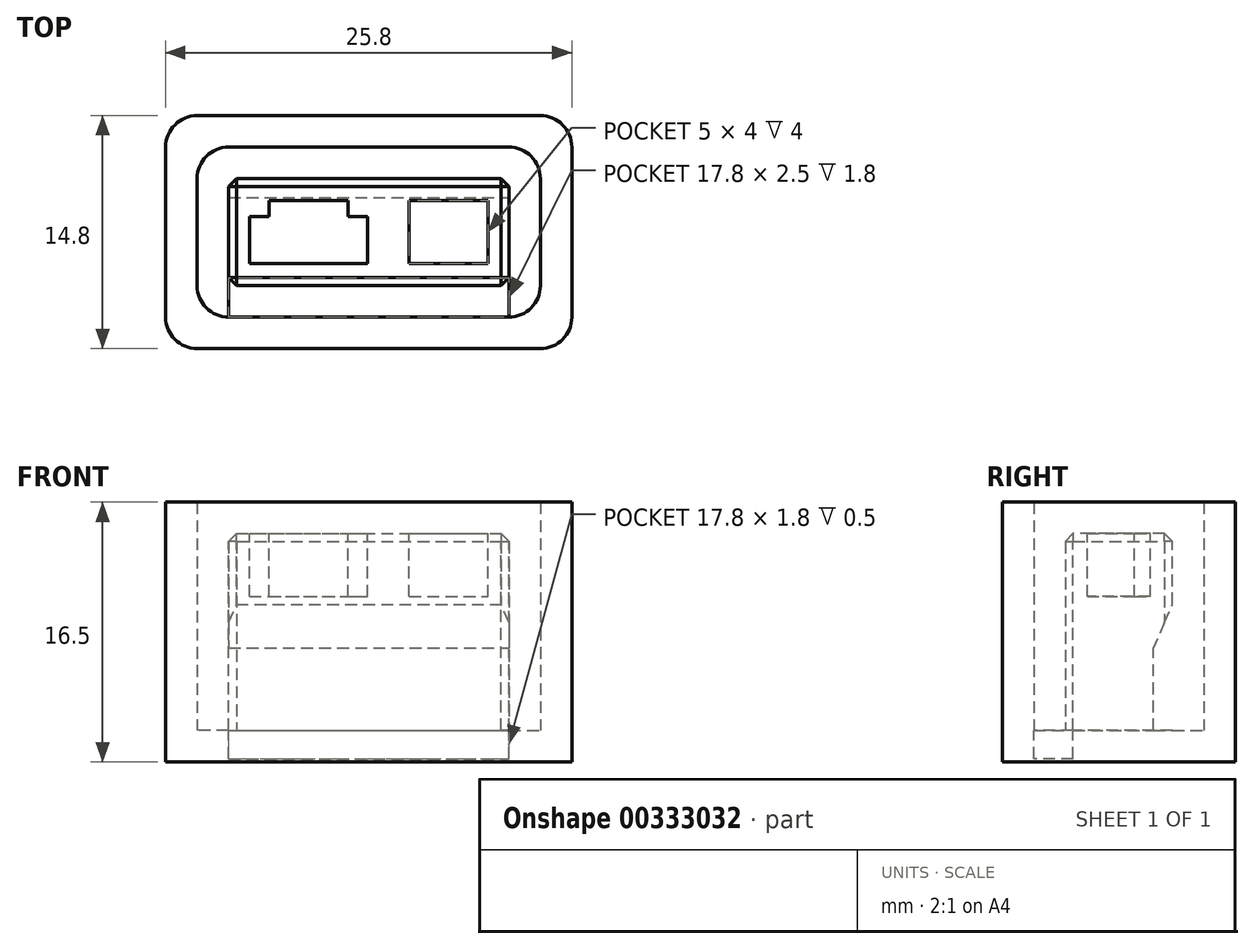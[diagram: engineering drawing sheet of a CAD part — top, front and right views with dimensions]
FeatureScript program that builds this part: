
annotation { "Feature Type Name" : "Feature", "Feature Type Description" : "" }
export const myFeature = defineFeature(function(context is Context, id is Id, definition is map)
    precondition{}
    {
        {
            var Q0;
            Q0=qCreatedBy(makeId("Top.planeOp"),FACE);
            var sketch = newSketch(context, id + "F0", { "sketchPlane" : qUnion([Q0])});
            skLineSegment(sketch, "E0.bottom", {"start": v(-12.9, 7.4) * mm, "end": v(12.9, 7.4) * mm});
            skLineSegment(sketch, "E0.top", {"start": v(-12.9, -7.4) * mm, "end": v(12.9, -7.4) * mm});
            skLineSegment(sketch, "E0.left", {"start": v(-12.9, 7.4) * mm, "end": v(-12.9, -7.4) * mm});
            skLineSegment(sketch, "E0.right", {"start": v(12.9, 7.4) * mm, "end": v(12.9, -7.4) * mm});
            skPoint(sketch, "E0.middle", {"position": v(0, 0) * mm});
            skSolve(sketch);
        }
        {
            var Q0;
            Q0 = qSketchRegion(id + "F0", true);
            extrude(context, id + "F1", {"entities" : qUnion([Q0]), "depth" : 2 * mm});
        }
        {
            var Q0;
            Q0=makeQuery(id+"F1.opExtrude","CAP_FACE",FACE,{"disambiguationData":[OSD([sQuery(id+"F0.wireOp",EDGE,"E0.bottom"),sQuery(id+"F0.wireOp",EDGE,"E0.top"),sQuery(id+"F0.wireOp",EDGE,"E0.left"),sQuery(id+"F0.wireOp",EDGE,"E0.right")])],"isStart":false});
            var sketch = newSketch(context, id + "F2", { "sketchPlane" : qUnion([Q0])});
            skLineSegment(sketch, "E1.bottom", {"start": v(-12.9, 7.4) * mm, "end": v(12.9, 7.4) * mm});
            skLineSegment(sketch, "E1.top", {"start": v(-12.9, -7.4) * mm, "end": v(12.9, -7.4) * mm});
            skLineSegment(sketch, "E1.left", {"start": v(-12.9, 7.4) * mm, "end": v(-12.9, -7.4) * mm});
            skLineSegment(sketch, "E1.right", {"start": v(12.9, 7.4) * mm, "end": v(12.9, -7.4) * mm});
            skPoint(sketch, "E1.middle", {"position": v(0, 0) * mm});
            skLineSegment(sketch, "E2.bottom", {"start": v(-10.9, 5.4) * mm, "end": v(10.9, 5.4) * mm});
            skLineSegment(sketch, "E2.top", {"start": v(-10.9, -5.4) * mm, "end": v(10.9, -5.4) * mm});
            skLineSegment(sketch, "E2.left", {"start": v(-10.9, 5.4) * mm, "end": v(-10.9, -5.4) * mm});
            skLineSegment(sketch, "E2.right", {"start": v(10.9, 5.4) * mm, "end": v(10.9, -5.4) * mm});
            skSolve(sketch);
        }
        {
            var Q0;
            Q0 = qSketchRegion(id + "F2", true);
            extrude(context, id + "F3", {"entities" : qUnion([Q0]), "operationType" : NewBodyOperationType.ADD, "depth" : 14.5 * mm});
        }
        {
            var Q0;
            Q0=makeQuery(id+"F1.opExtrude","CAP_FACE",FACE,{"disambiguationData":[OSD([sQuery(id+"F0.wireOp",EDGE,"E0.bottom"),sQuery(id+"F0.wireOp",EDGE,"E0.top"),sQuery(id+"F0.wireOp",EDGE,"E0.left"),sQuery(id+"F0.wireOp",EDGE,"E0.right")])],"isStart":false});
            var sketch = newSketch(context, id + "F4", { "sketchPlane" : qUnion([Q0])});
            skLineSegment(sketch, "E3.bottom", {"start": v(-8.9, 3.4) * mm, "end": v(8.9, 3.4) * mm});
            skLineSegment(sketch, "E3.top", {"start": v(-8.9, -3.4) * mm, "end": v(8.9, -3.4) * mm});
            skLineSegment(sketch, "E3.left", {"start": v(-8.9, 3.4) * mm, "end": v(-8.9, -3.4) * mm});
            skLineSegment(sketch, "E3.right", {"start": v(8.9, 3.4) * mm, "end": v(8.9, -3.4) * mm});
            skPoint(sketch, "E3.middle", {"position": v(0, 0) * mm});
            skSolve(sketch);
        }
        {
            var Q0;
            Q0 = qSketchRegion(id + "F4", true);
            extrude(context, id + "F5", {"entities" : qUnion([Q0]), "operationType" : NewBodyOperationType.ADD, "depth" : 12.5 * mm});
        }
        {
            var Q0;
            Q0=makeQuery(id+"F5.opExtrude","SWEPT_FACE",FACE,{"disambiguationData":[OSD([sQuery(id+"F4.wireOp",EDGE,"E3.right")])]});
            var sketch = newSketch(context, id + "F6", { "sketchPlane" : qUnion([Q0])});
            skLineSegment(sketch, "E4.bottom", {"start": v(3.4, 2) * mm, "end": v(2.2, 2) * mm});
            skLineSegment(sketch, "E4.left", {"start": v(3.4, 2) * mm, "end": v(3.4, 10) * mm});
            skLineSegment(sketch, "E4.right", {"start": v(2.2, 2) * mm, "end": v(2.2, 7.25) * mm});
            skLineSegment(sketch, "E5", {"start": v(3.4, 10) * mm, "end": v(2.2, 7.25) * mm});
            skSolve(sketch);
        }
        {
            var Q0;
            Q0 = qSketchRegion(id + "F6", true);
            extrude(context, id + "F7", {"entities" : qUnion([Q0]), "operationType" : NewBodyOperationType.REMOVE, "oppositeDirection" : true, "depth" : 17.8 * mm});
        }
        {
            var Q0;
            Q0=makeQuery(id+"F5.opExtrude","CAP_FACE",FACE,{"disambiguationData":[OSD([sQuery(id+"F4.wireOp",EDGE,"E3.bottom"),sQuery(id+"F4.wireOp",EDGE,"E3.top"),sQuery(id+"F4.wireOp",EDGE,"E3.left"),sQuery(id+"F4.wireOp",EDGE,"E3.right")])],"isStart":false});
            var Q1;
            Q1=makeQuery(id+"F5.opExtrude","SWEPT_EDGE",EDGE,{"disambiguationData":[OSD([sQuery(id+"F4.wireOp",EDGE,"E3.top"),sQuery(id+"F4.wireOp",EDGE,"E3.left")])]});
            var Q2;
            Q2=makeQuery(id+"F5.opExtrude","SWEPT_EDGE",EDGE,{"disambiguationData":[OSD([sQuery(id+"F4.wireOp",EDGE,"E3.top"),sQuery(id+"F4.wireOp",EDGE,"E3.right")])]});
            var Q3;
            Q3=makeQuery(id+"F5.opExtrude","SWEPT_EDGE",EDGE,{"disambiguationData":[OSD([sQuery(id+"F4.wireOp",EDGE,"E3.bottom"),sQuery(id+"F4.wireOp",EDGE,"E3.right")])]});
            var Q4;
            Q4=makeQuery(id+"F5.opExtrude","SWEPT_EDGE",EDGE,{"disambiguationData":[OSD([sQuery(id+"F4.wireOp",EDGE,"E3.bottom"),sQuery(id+"F4.wireOp",EDGE,"E3.left")])]});
            var Q5;
            Q5=makeQuery(id+"F7.boolean.opBoolean","COPY",EDGE,{"derivedFrom":makeQuery(id+"F7.opExtrude","CAP_EDGE",EDGE,{"disambiguationData":[OSD([sQuery(id+"F6.wireOp",EDGE,"E4.right")])],"isStart":false})});
            var Q6;
            Q6=makeQuery(id+"F7.boolean.opBoolean","COPY",EDGE,{"derivedFrom":makeQuery(id+"F7.opExtrude","CAP_EDGE",EDGE,{"disambiguationData":[OSD([sQuery(id+"F6.wireOp",EDGE,"E5")])],"isStart":false})});
            var Q7;
            Q7=makeQuery(id+"F7.boolean.opBoolean","COPY",EDGE,{"derivedFrom":makeQuery(id+"F7.opExtrude","CAP_EDGE",EDGE,{"disambiguationData":[OSD([sQuery(id+"F6.wireOp",EDGE,"E4.right")])],"isStart":true})});
            var Q8;
            Q8=makeQuery(id+"F7.boolean.opBoolean","COPY",EDGE,{"derivedFrom":makeQuery(id+"F7.opExtrude","CAP_EDGE",EDGE,{"disambiguationData":[OSD([sQuery(id+"F6.wireOp",EDGE,"E5")])],"isStart":true})});
            chamfer(context, id + "F8", {"entities" : qUnion([Q0, Q1, Q2, Q3, Q4, Q5, Q6, Q7, Q8]), "width" : .5 * mm, "tangentPropagation" : true});
        }
        {
            var Q0;
            Q0=makeQuery(id+"F3.boolean.opBoolean","MERGE",EDGE,{"derivedFrom":[makeQuery(id+"F1.opExtrude","SWEPT_EDGE",EDGE,{"disambiguationData":[OSD([sQuery(id+"F0.wireOp",EDGE,"E0.bottom"),sQuery(id+"F0.wireOp",EDGE,"E0.left")])]}),makeQuery(id+"F3.opExtrude","SWEPT_EDGE",EDGE,{"disambiguationData":[OSD([sQuery(id+"F2.wireOp",EDGE,"E1.bottom"),sQuery(id+"F2.wireOp",EDGE,"E1.left")])]})]});
            var Q1;
            Q1=makeQuery(id+"F3.boolean.opBoolean","MERGE",EDGE,{"derivedFrom":[makeQuery(id+"F1.opExtrude","SWEPT_EDGE",EDGE,{"disambiguationData":[OSD([sQuery(id+"F0.wireOp",EDGE,"E0.bottom"),sQuery(id+"F0.wireOp",EDGE,"E0.right")])]}),makeQuery(id+"F3.opExtrude","SWEPT_EDGE",EDGE,{"disambiguationData":[OSD([sQuery(id+"F2.wireOp",EDGE,"E1.bottom"),sQuery(id+"F2.wireOp",EDGE,"E1.right")])]})]});
            var Q2;
            Q2=makeQuery(id+"F3.opExtrude","SWEPT_EDGE",EDGE,{"disambiguationData":[OSD([sQuery(id+"F2.wireOp",EDGE,"E2.bottom"),sQuery(id+"F2.wireOp",EDGE,"E2.right")])]});
            var Q3;
            Q3=makeQuery(id+"F3.opExtrude","SWEPT_EDGE",EDGE,{"disambiguationData":[OSD([sQuery(id+"F2.wireOp",EDGE,"E2.bottom"),sQuery(id+"F2.wireOp",EDGE,"E2.left")])]});
            var Q4;
            Q4=makeQuery(id+"F3.opExtrude","SWEPT_EDGE",EDGE,{"disambiguationData":[OSD([sQuery(id+"F2.wireOp",EDGE,"E2.top"),sQuery(id+"F2.wireOp",EDGE,"E2.right")])]});
            var Q5;
            Q5=makeQuery(id+"F3.opExtrude","SWEPT_EDGE",EDGE,{"disambiguationData":[OSD([sQuery(id+"F2.wireOp",EDGE,"E2.top"),sQuery(id+"F2.wireOp",EDGE,"E2.left")])]});
            var Q6;
            Q6=makeQuery(id+"F3.boolean.opBoolean","MERGE",EDGE,{"derivedFrom":[makeQuery(id+"F1.opExtrude","SWEPT_EDGE",EDGE,{"disambiguationData":[OSD([sQuery(id+"F0.wireOp",EDGE,"E0.top"),sQuery(id+"F0.wireOp",EDGE,"E0.left")])]}),makeQuery(id+"F3.opExtrude","SWEPT_EDGE",EDGE,{"disambiguationData":[OSD([sQuery(id+"F2.wireOp",EDGE,"E1.top"),sQuery(id+"F2.wireOp",EDGE,"E1.left")])]})]});
            var Q7;
            Q7=makeQuery(id+"F3.boolean.opBoolean","MERGE",EDGE,{"derivedFrom":[makeQuery(id+"F1.opExtrude","SWEPT_EDGE",EDGE,{"disambiguationData":[OSD([sQuery(id+"F0.wireOp",EDGE,"E0.top"),sQuery(id+"F0.wireOp",EDGE,"E0.right")])]}),makeQuery(id+"F3.opExtrude","SWEPT_EDGE",EDGE,{"disambiguationData":[OSD([sQuery(id+"F2.wireOp",EDGE,"E1.top"),sQuery(id+"F2.wireOp",EDGE,"E1.right")])]})]});
            fillet(context, id + "F9", {"entities" : qUnion([Q0, Q1, Q2, Q3, Q4, Q5, Q6, Q7]), "radius" : 2 * mm, "tangentPropagation" : true, "allowEdgeOverflow" : false});
        }
        {
            var Q0;
            Q0=makeQuery(id+"F3.opExtrude","CAP_FACE",FACE,{"disambiguationData":[OSD([sQuery(id+"F2.wireOp",EDGE,"E1.bottom"),sQuery(id+"F2.wireOp",EDGE,"E1.top"),sQuery(id+"F2.wireOp",EDGE,"E1.left"),sQuery(id+"F2.wireOp",EDGE,"E1.right"),sQuery(id+"F2.wireOp",EDGE,"E2.bottom"),sQuery(id+"F2.wireOp",EDGE,"E2.top"),sQuery(id+"F2.wireOp",EDGE,"E2.left"),sQuery(id+"F2.wireOp",EDGE,"E2.right")])],"isStart":false});
            var sketch = newSketch(context, id + "F10", { "sketchPlane" : qUnion([Q0])});
            skLineSegment(sketch, "E6.bottom", {"start": v(-7.58, -2) * mm, "end": v(-0.08, -2) * mm});
            skLineSegment(sketch, "E6.top", {"start": v(-7.58, 1) * mm, "end": v(-6.33, 1) * mm});
            skLineSegment(sketch, "E6.left", {"start": v(-7.58, -2) * mm, "end": v(-7.58, 1) * mm});
            skLineSegment(sketch, "E6.right", {"start": v(-0.08, -2) * mm, "end": v(-0.08, 1) * mm});
            skLineSegment(sketch, "E7.top", {"start": v(-6.33, 2) * mm, "end": v(-1.32, 2) * mm});
            skLineSegment(sketch, "E7.left", {"start": v(-6.33, 1) * mm, "end": v(-6.33, 2) * mm});
            skLineSegment(sketch, "E7.right", {"start": v(-1.33, 1) * mm, "end": v(-1.33, 2) * mm});
            skLineSegment(sketch, "E8.trimOffspring", {"start": v(-1.33, 1) * mm, "end": v(-0.08, 1) * mm});
            skLineSegment(sketch, "E9.bottom", {"start": v(2.58, 2) * mm, "end": v(7.58, 2) * mm});
            skLineSegment(sketch, "E9.top", {"start": v(2.57, -2) * mm, "end": v(7.58, -2) * mm});
            skLineSegment(sketch, "E9.left", {"start": v(2.58, 2) * mm, "end": v(2.57, -2) * mm});
            skLineSegment(sketch, "E9.right", {"start": v(7.58, 2) * mm, "end": v(7.58, -2) * mm});
            skSolve(sketch);
        }
        {
            var Q0;
            Q0 = qSketchRegion(id + "F10", true);
            extrude(context, id + "F11", {"entities" : qUnion([Q0]), "operationType" : NewBodyOperationType.REMOVE, "oppositeDirection" : true, "depth" : 6 * mm});
        }
        {
            var Q0;
            Q0=makeQuery(id+"F1.opExtrude","CAP_FACE",FACE,{"disambiguationData":[OSD([sQuery(id+"F0.wireOp",EDGE,"E0.bottom"),sQuery(id+"F0.wireOp",EDGE,"E0.top"),sQuery(id+"F0.wireOp",EDGE,"E0.left"),sQuery(id+"F0.wireOp",EDGE,"E0.right")])],"isStart":false});
            var sketch = newSketch(context, id + "F12", { "sketchPlane" : qUnion([Q0])});
            skLineSegment(sketch, "E10.bottom", {"start": v(-8.9, -2.9) * mm, "end": v(8.9, -2.9) * mm});
            skLineSegment(sketch, "E10.top", {"start": v(-8.9, -5.4) * mm, "end": v(8.9, -5.4) * mm});
            skLineSegment(sketch, "E10.left", {"start": v(-8.9, -2.9) * mm, "end": v(-8.9, -5.4) * mm});
            skLineSegment(sketch, "E10.right", {"start": v(8.9, -2.9) * mm, "end": v(8.9, -5.4) * mm});
            skLineSegment(sketch, "E11", {"start": v(8.9, -3.4) * mm, "end": v(-8.9, -3.4) * mm});
            skSolve(sketch);
        }
        {
            var Q0;
            Q0 = qSketchRegion(id + "F12", true);
            extrude(context, id + "F13", {"entities" : qUnion([Q0]), "operationType" : NewBodyOperationType.REMOVE, "oppositeDirection" : true, "depth" : 1.8 * mm});
        }
    });
